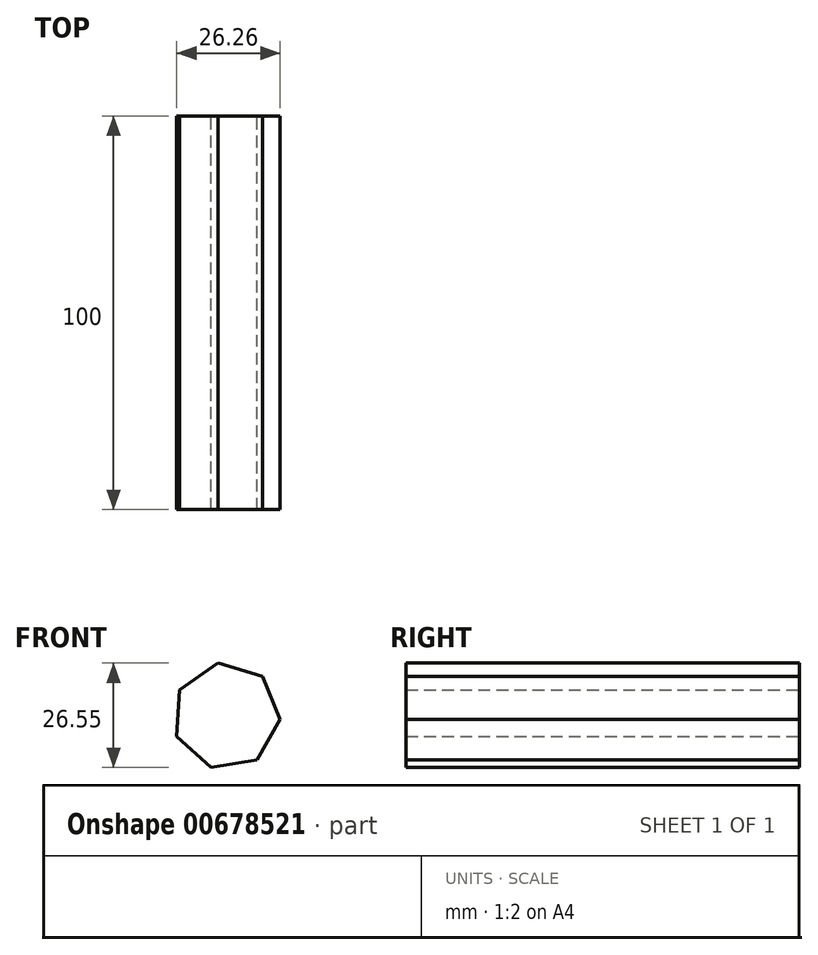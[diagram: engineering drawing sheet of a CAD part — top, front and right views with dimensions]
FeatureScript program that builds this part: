
annotation { "Feature Type Name" : "Feature", "Feature Type Description" : "" }
export const myFeature = defineFeature(function(context is Context, id is Id, definition is map)
    precondition{}
    {
        {
            var Q0;
            Q0=qCreatedBy(makeId("Front.planeOp"),FACE);
            var sketch = newSketch(context, id + "F0", { "sketchPlane" : qUnion([Q0])});
            skLineSegment(sketch, "E0.0", {"start": v(-3.88, -13.08) * mm, "end": v(-12.64, -5.13) * mm});
            skLineSegment(sketch, "E0.1", {"start": v(-12.64, -5.13) * mm, "end": v(-11.9, 6.69) * mm});
            skLineSegment(sketch, "E0.2", {"start": v(-11.9, 6.69) * mm, "end": v(-2.19, 13.47) * mm});
            skLineSegment(sketch, "E0.3", {"start": v(-2.19, 13.47) * mm, "end": v(9.17, 10.1) * mm});
            skLineSegment(sketch, "E0.4", {"start": v(9.17, 10.1) * mm, "end": v(13.62, -0.87) * mm});
            skLineSegment(sketch, "E0.5", {"start": v(13.62, -0.87) * mm, "end": v(7.81, -11.19) * mm});
            skLineSegment(sketch, "E0.6", {"start": v(7.81, -11.19) * mm, "end": v(-3.88, -13.08) * mm});
            skSolve(sketch);
        }
        {
            var Q0;
            Q0=makeQuery(id+"F0.imprint","IMPRINT",FACE,{"disambiguationData":[TD([[makeQuery(id+"F0.imprint","IMPRINT",EDGE,{"derivedFrom":sQuery(id+"F0.wireOp",EDGE,"E0.0")}),-1.0]])]});
            extrude(context, id + "F1", {"entities" : qUnion([Q0]), "depth" : 100 * mm, "offsetDistance" : 25 * mm});
        }
    });
